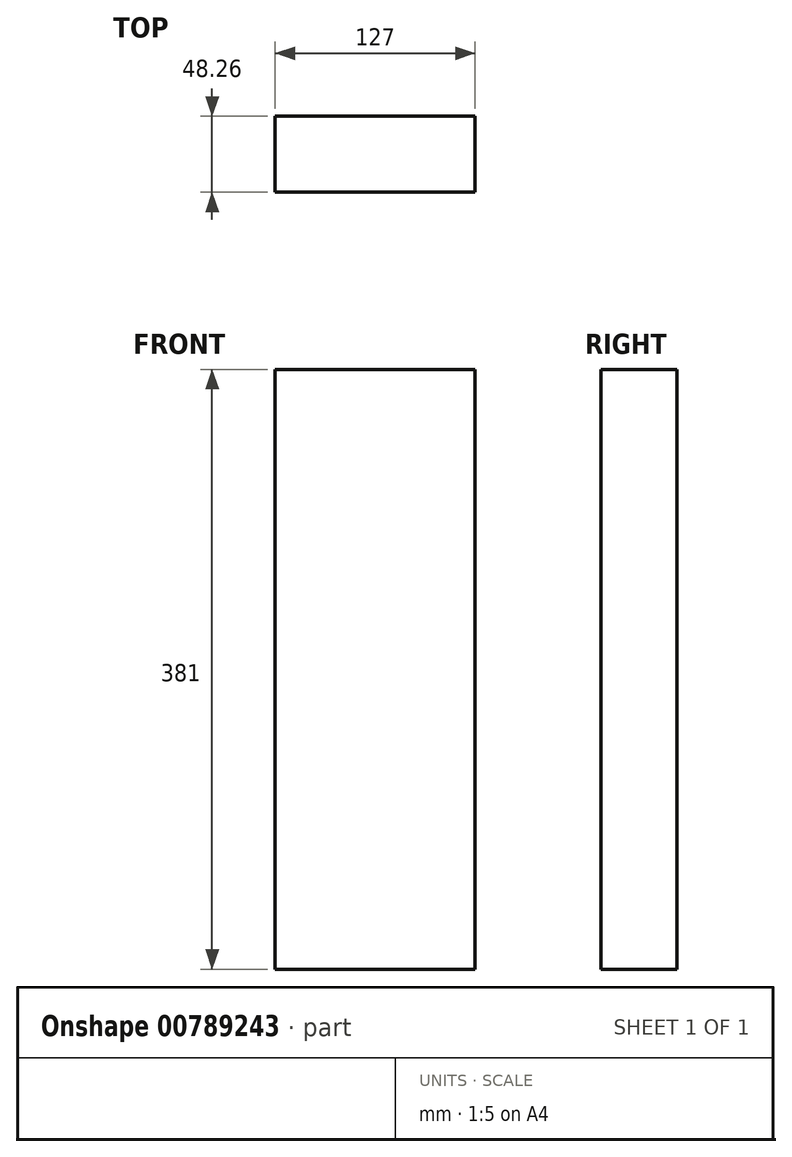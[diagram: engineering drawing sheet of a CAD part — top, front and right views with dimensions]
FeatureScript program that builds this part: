
annotation { "Feature Type Name" : "Feature", "Feature Type Description" : "" }
export const myFeature = defineFeature(function(context is Context, id is Id, definition is map)
    precondition{}
    {
        {
            var Q0;
            Q0=qCreatedBy(makeId("Front.planeOp"),FACE);
            var sketch = newSketch(context, id + "F0", { "sketchPlane" : qUnion([Q0])});
            skLineSegment(sketch, "E0.bottom", {"start": v(0, 0) * mm, "end": v(127, 0) * mm});
            skLineSegment(sketch, "E0.top", {"start": v(0, 381) * mm, "end": v(127, 381) * mm});
            skLineSegment(sketch, "E0.left", {"start": v(0, 0) * mm, "end": v(0, 381) * mm});
            skLineSegment(sketch, "E0.right", {"start": v(127, 0) * mm, "end": v(127, 381) * mm});
            skSolve(sketch);
        }
        {
            var Q0;
            Q0 = qSketchRegion(id + "F0", true);
            extrude(context, id + "F1", {"entities" : qUnion([Q0]), "depth" : 48.26 * mm, "offsetDistance" : 25.4 * mm});
        }
    });
